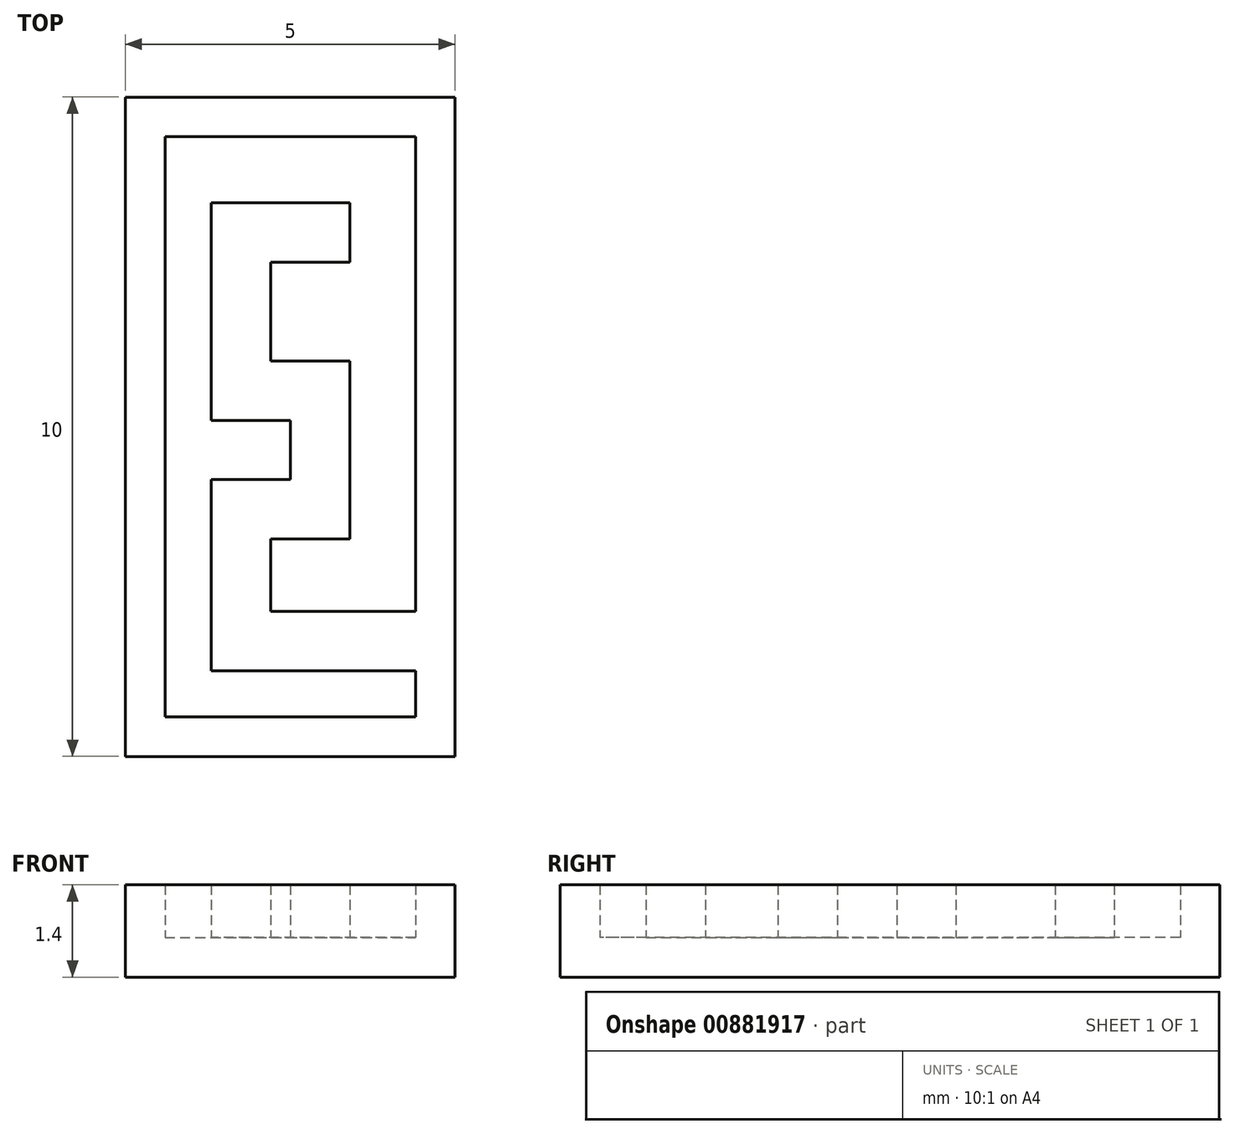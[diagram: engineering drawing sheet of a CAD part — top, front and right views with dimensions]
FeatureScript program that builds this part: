
annotation { "Feature Type Name" : "Feature", "Feature Type Description" : "" }
export const myFeature = defineFeature(function(context is Context, id is Id, definition is map)
    precondition{}
    {
        {
            var Q0;
            Q0=qCreatedBy(makeId("Top.planeOp"),FACE);
            var sketch = newSketch(context, id + "F0", { "sketchPlane" : qUnion([Q0])});
            skLineSegment(sketch, "E0.bottom", {"start": v(2.44, 6.63) * mm, "end": v(7.44, 6.63) * mm});
            skLineSegment(sketch, "E0.top", {"start": v(2.44, -3.37) * mm, "end": v(7.44, -3.37) * mm});
            skLineSegment(sketch, "E0.left", {"start": v(2.44, 6.63) * mm, "end": v(2.44, -3.37) * mm});
            skLineSegment(sketch, "E0.right", {"start": v(7.44, 6.63) * mm, "end": v(7.44, -3.37) * mm});
            skSolve(sketch);
        }
        {
            var Q0;
            Q0=makeQuery(id+"F0.imprint","IMPRINT",FACE,{"disambiguationData":[TD([[makeQuery(id+"F0.imprint","IMPRINT",EDGE,{"derivedFrom":sQuery(id+"F0.wireOp",EDGE,"E0.bottom")}),-1.0]])]});
            extrude(context, id + "F1", {"entities" : qUnion([Q0]), "depth" : 1.4 * mm, "offsetDistance" : 25.4 * mm});
        }
        {
            var Q0;
            Q0=makeQuery(id+"F1.opExtrude","CAP_FACE",FACE,{"disambiguationData":[OSD([sQuery(id+"F0.wireOp",EDGE,"E0.bottom"),sQuery(id+"F0.wireOp",EDGE,"E0.top"),sQuery(id+"F0.wireOp",EDGE,"E0.left"),sQuery(id+"F0.wireOp",EDGE,"E0.right")])],"isStart":false});
            shell(context, id + "F2", {"entities" : qUnion([Q0]), "thickness" : 0.6 * mm});
        }
        {
            var Q0;
            Q0=makeQuery(id+"F2.opShell","OFFSET_FACE",FACE,{"disambiguationData":[OSD([sQuery(id+"F0.wireOp",EDGE,"E0.bottom"),sQuery(id+"F0.wireOp",EDGE,"E0.top"),sQuery(id+"F0.wireOp",EDGE,"E0.left"),sQuery(id+"F0.wireOp",EDGE,"E0.right")])]});
            var sketch = newSketch(context, id + "F3", { "sketchPlane" : qUnion([Q0])});
            skLineSegment(sketch, "E1", {"start": v(6.84, -1.17) * mm, "end": v(4.64, -1.17) * mm});
            skLineSegment(sketch, "E2", {"start": v(4.64, -1.17) * mm, "end": v(4.64, -1.17) * mm});
            skLineSegment(sketch, "E3", {"start": v(4.64, -1.17) * mm, "end": v(4.64, -0.07) * mm});
            skLineSegment(sketch, "E4", {"start": v(4.64, -0.07) * mm, "end": v(5.84, -0.07) * mm});
            skLineSegment(sketch, "E5", {"start": v(5.84, -0.07) * mm, "end": v(5.84, 2.63) * mm});
            skLineSegment(sketch, "E6", {"start": v(5.84, 2.63) * mm, "end": v(4.64, 2.63) * mm});
            skLineSegment(sketch, "E7", {"start": v(4.64, 2.63) * mm, "end": v(4.64, 4.13) * mm});
            skLineSegment(sketch, "E8", {"start": v(4.64, 4.13) * mm, "end": v(5.84, 4.13) * mm});
            skLineSegment(sketch, "E9.2", {"start": v(3.74, 1.73) * mm, "end": v(3.74, 5.03) * mm});
            skLineSegment(sketch, "E9.3", {"start": v(4.94, 1.73) * mm, "end": v(3.74, 1.73) * mm});
            skLineSegment(sketch, "E9.4", {"start": v(6.84, -2.07) * mm, "end": v(3.74, -2.07) * mm});
            skLineSegment(sketch, "E9.5", {"start": v(3.74, -2.07) * mm, "end": v(3.74, 0.83) * mm});
            skLineSegment(sketch, "E9.6", {"start": v(3.74, 0.83) * mm, "end": v(4.94, 0.83) * mm});
            skLineSegment(sketch, "E9.7", {"start": v(4.94, 0.83) * mm, "end": v(4.94, 1.73) * mm});
            skLineSegment(sketch, "E10", {"start": v(5.84, 4.13) * mm, "end": v(5.84, 5.03) * mm});
            skLineSegment(sketch, "E11", {"start": v(3.74, 5.03) * mm, "end": v(5.84, 5.03) * mm});
            skSolve(sketch);
        }
        {
            var Q0;
            {var subQ2=sQuery(id+"F3.wireOp",EDGE,"E1");Q0=makeQuery(id+"F3.imprint","IMPRINT",FACE,{"disambiguationData":[TD([[makeQuery(id+"F3.imprint","IMPRINT",EDGE,{"derivedFrom":subQ2}),1.0]])]});}
            extrude(context, id + "F4", {"entities" : qUnion([Q0]), "operationType" : NewBodyOperationType.ADD, "depth" : 0.8 * mm, "offsetDistance" : 25 * mm});
        }
    });
